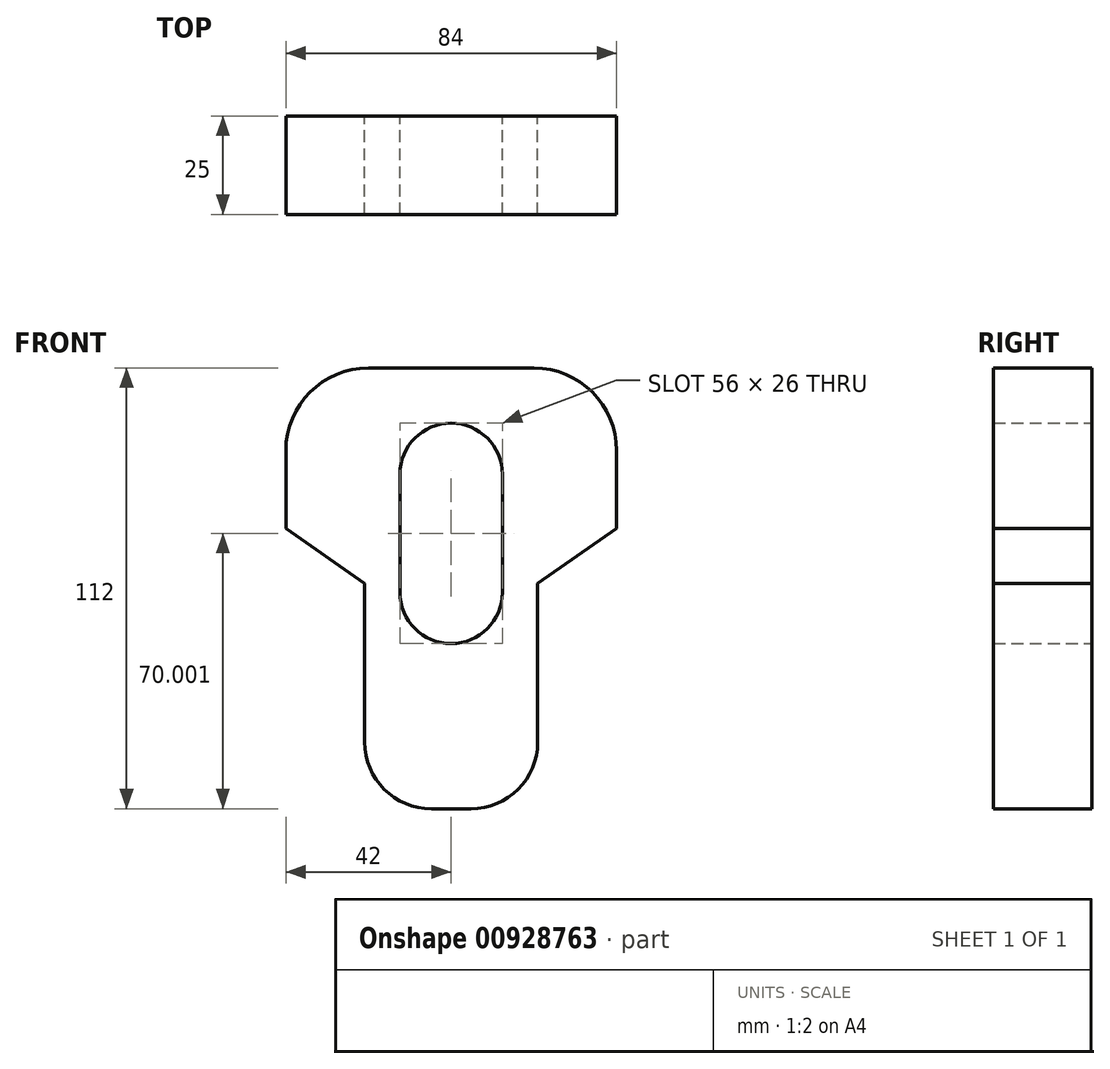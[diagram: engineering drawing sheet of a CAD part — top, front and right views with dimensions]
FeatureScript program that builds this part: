
annotation { "Feature Type Name" : "Feature", "Feature Type Description" : "" }
export const myFeature = defineFeature(function(context is Context, id is Id, definition is map)
    precondition{}
    {
        {
            var Q0;
            Q0=qCreatedBy(makeId("Front.planeOp"),FACE);
            var sketch = newSketch(context, id + "F0", { "sketchPlane" : qUnion([Q0])});
            skLineSegment(sketch, "E0", {"start": v(-22, -14.84) * mm, "end": v(-22, 25.36) * mm});
            skLineSegment(sketch, "E1", {"start": v(-22, 25.36) * mm, "end": v(-42, 39.36) * mm});
            skLineSegment(sketch, "E2", {"start": v(-42, 39.36) * mm, "end": v(-42, 59.16) * mm});
            skArc(sketch, "E3", {"start": v(-42, 59.16) * mm, "mid": v(-35.85, 74.01) * mm, "end": v(-21, 80.16) * mm});
            skArc(sketch, "E4", {"start": v(-22, -14.84) * mm, "mid": v(-17.02, -26.86) * mm, "end": v(-5, -31.84) * mm});
            skLineSegment(sketch, "E5", {"start": v(-21, 80.16) * mm, "end": v(0, 80.16) * mm});
            skLineSegment(sketch, "E6", {"start": v(-5, -31.84) * mm, "end": v(0, -31.84) * mm});
            skArc(sketch, "E7", {"start": v(0, 66.16) * mm, "mid": v(-9.2, 62.35) * mm, "end": v(-13, 53.16) * mm});
            skArc(sketch, "E8", {"start": v(-13, 23.16) * mm, "mid": v(-9.2, 13.97) * mm, "end": v(0, 10.16) * mm});
            skLineSegment(sketch, "E9", {"start": v(-13, 23.16) * mm, "end": v(-13, 53.16) * mm});
            skLineSegment(sketch, "E10", {"start": v(0, 66.16) * mm, "end": v(0, 10.16) * mm});
            skLineSegment(sketch, "E11", {"start": v(-22, 25.36) * mm, "end": v(-22, 112.8) * mm, "construction": true});
            skLineSegment(sketch, "E12.MirrorCS", {"start": v(5, -31.84) * mm, "end": v(0, -31.84) * mm});
            skLineSegment(sketch, "E13.MirrorCS", {"start": v(22, 25.36) * mm, "end": v(42, 39.36) * mm});
            skArc(sketch, "E14.MirrorCS", {"start": v(0, 66.16) * mm, "mid": v(9.2, 62.35) * mm, "end": v(13, 53.16) * mm});
            skLineSegment(sketch, "E15.MirrorCS", {"start": v(42, 39.36) * mm, "end": v(42, 59.16) * mm});
            skLineSegment(sketch, "E16.MirrorCS", {"start": v(22, -14.84) * mm, "end": v(22, 25.36) * mm});
            skArc(sketch, "E17.MirrorCS", {"start": v(13, 23.16) * mm, "mid": v(9.2, 13.97) * mm, "end": v(0, 10.16) * mm});
            skArc(sketch, "E18.MirrorCS", {"start": v(42, 59.16) * mm, "mid": v(35.85, 74.01) * mm, "end": v(21, 80.16) * mm});
            skLineSegment(sketch, "E19.MirrorCS", {"start": v(21, 80.16) * mm, "end": v(0, 80.16) * mm});
            skLineSegment(sketch, "E20.MirrorCS", {"start": v(13, 23.16) * mm, "end": v(13, 53.16) * mm});
            skArc(sketch, "E21.MirrorCS", {"start": v(22, -14.84) * mm, "mid": v(17.02, -26.86) * mm, "end": v(5, -31.84) * mm});
            skSolve(sketch);
        }
        {
            var Q0;
            Q0 = qSketchRegion(id + "F0", true);
            extrude(context, id + "F1", {"entities" : qUnion([Q0]), "depth" : 25 * mm, "offsetDistance" : 25 * mm});
        }
    });
